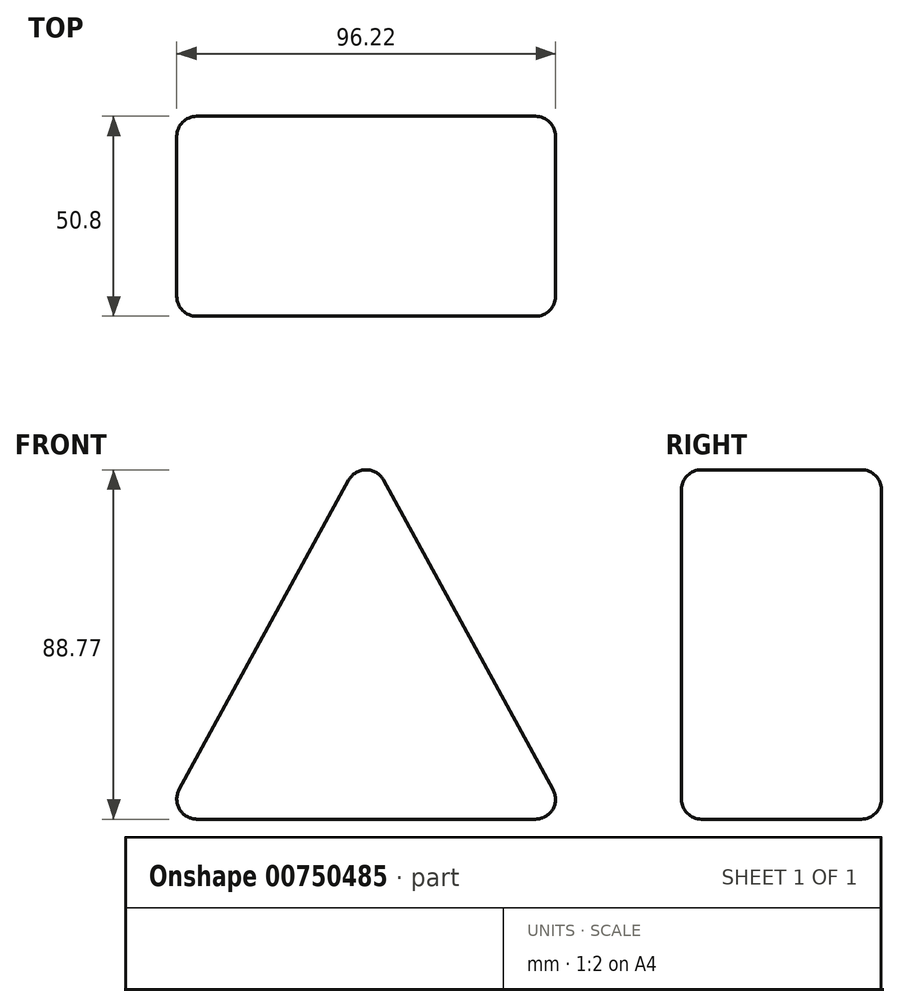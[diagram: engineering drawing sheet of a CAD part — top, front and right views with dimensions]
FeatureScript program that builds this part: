
annotation { "Feature Type Name" : "Feature", "Feature Type Description" : "" }
export const myFeature = defineFeature(function(context is Context, id is Id, definition is map)
    precondition{}
    {
        {
            var Q0;
            Q0=qCreatedBy(makeId("Front.planeOp"),FACE);
            var sketch = newSketch(context, id + "F0", { "sketchPlane" : qUnion([Q0])});
            skLineSegment(sketch, "E0", {"start": v(-51.6, -41.37) * mm, "end": v(0, 52.9) * mm});
            skLineSegment(sketch, "E1", {"start": v(0, 52.9) * mm, "end": v(51.6, -41.37) * mm});
            skLineSegment(sketch, "E2", {"start": v(51.6, -41.37) * mm, "end": v(-51.6, -41.37) * mm});
            skSolve(sketch);
        }
        {
            var Q0;
            Q0 = qSketchRegion(id + "F0", true);
            extrude(context, id + "F1", {"entities" : qUnion([Q0]), "depth" : 50.8 * mm, "offsetDistance" : 25.4 * mm});
        }
        {
            var Q0;
            Q0=makeQuery(id+"F1.opExtrude","SWEPT_FACE",FACE,{"disambiguationData":[OSD([sQuery(id+"F0.wireOp",EDGE,"E1")])]});
            var Q1;
            Q1=makeQuery(id+"F1.opExtrude","CAP_FACE",FACE,{"disambiguationData":[OSD([sQuery(id+"F0.wireOp",EDGE,"E0"),sQuery(id+"F0.wireOp",EDGE,"E1"),sQuery(id+"F0.wireOp",EDGE,"E2")])],"isStart":true});
            var Q2;
            Q2=makeQuery(id+"F1.opExtrude","CAP_EDGE",EDGE,{"disambiguationData":[OSD([sQuery(id+"F0.wireOp",EDGE,"E0")])],"isStart":false});
            var Q3;
            Q3=makeQuery(id+"F1.opExtrude","CAP_FACE",FACE,{"disambiguationData":[OSD([sQuery(id+"F0.wireOp",EDGE,"E0"),sQuery(id+"F0.wireOp",EDGE,"E1"),sQuery(id+"F0.wireOp",EDGE,"E2")])],"isStart":false});
            var Q4;
            Q4=makeQuery(id+"F1.opExtrude","CAP_EDGE",EDGE,{"disambiguationData":[OSD([sQuery(id+"F0.wireOp",EDGE,"E2")])],"isStart":false});
            var Q5;
            Q5=makeQuery(id+"F1.opExtrude","CAP_EDGE",EDGE,{"disambiguationData":[OSD([sQuery(id+"F0.wireOp",EDGE,"E1")])],"isStart":false});
            var Q6;
            Q6=makeQuery(id+"F1.opExtrude","SWEPT_EDGE",EDGE,{"disambiguationData":[OSD([sQuery(id+"F0.wireOp",EDGE,"E0"),sQuery(id+"F0.wireOp",EDGE,"E2")])]});
            fillet(context, id + "F2", {"entities" : qUnion([Q0, Q1, Q2, Q3, Q4, Q5, Q6]), "radius" : 5.08 * mm, "tangentPropagation" : true, "allowEdgeOverflow" : false});
        }
    });
